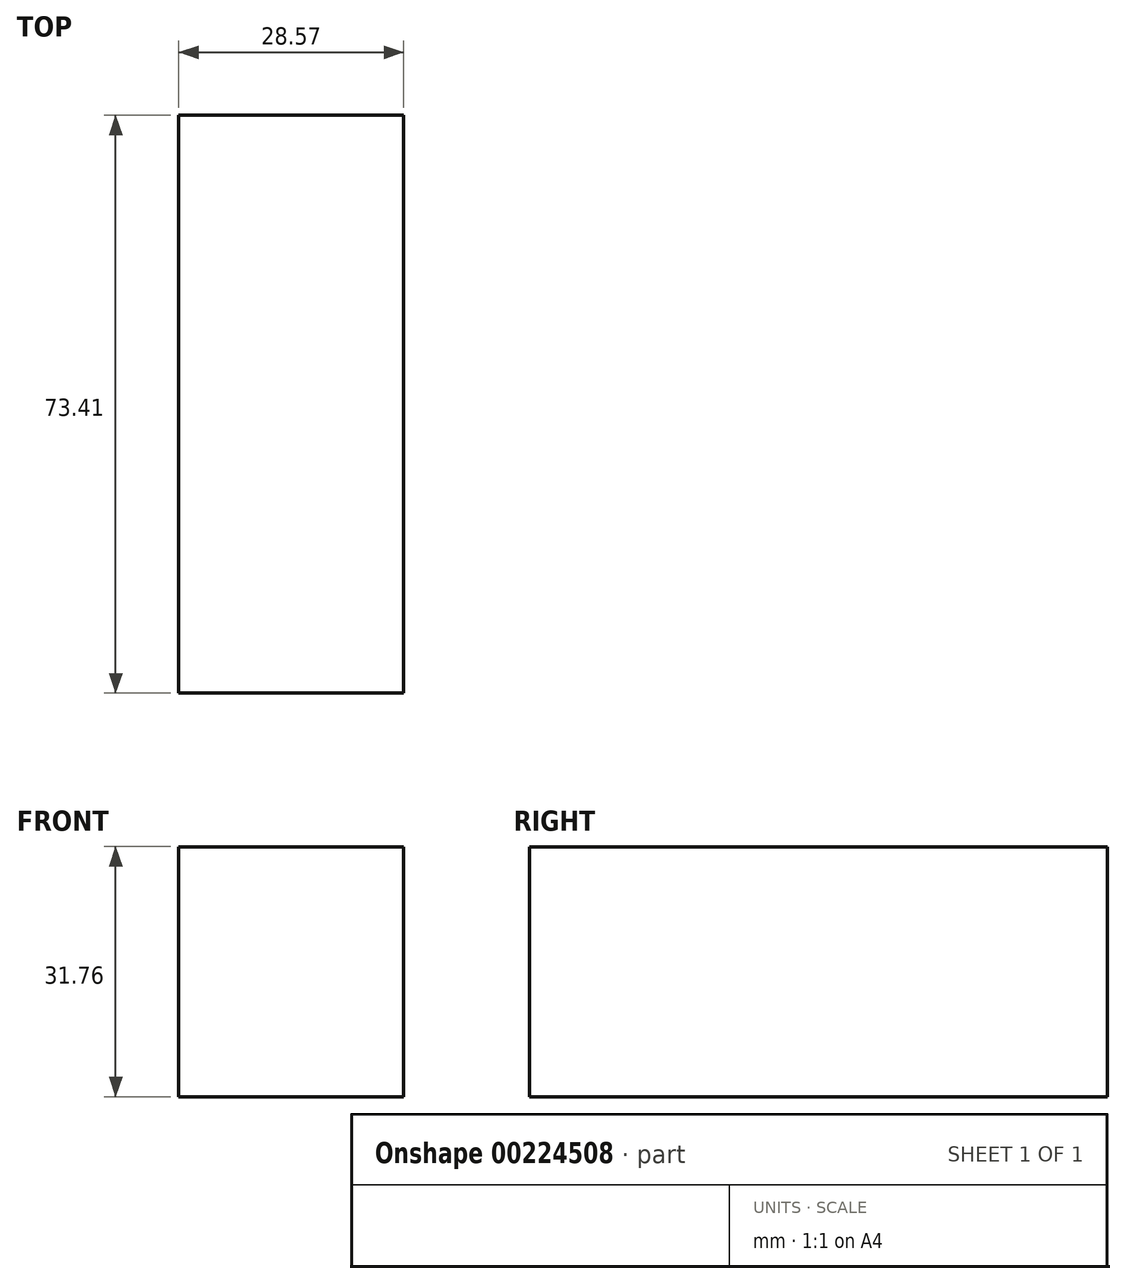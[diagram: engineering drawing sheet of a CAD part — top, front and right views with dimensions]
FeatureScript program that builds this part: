
annotation { "Feature Type Name" : "Feature", "Feature Type Description" : "" }
export const myFeature = defineFeature(function(context is Context, id is Id, definition is map)
    precondition{}
    {
        {
            var Q0;
            Q0=qCreatedBy(makeId("Front.planeOp"),FACE);
            var sketch = newSketch(context, id + "F0", { "sketchPlane" : qUnion([Q0])});
            skLineSegment(sketch, "E0", {"start": v(0, 0) * mm, "end": v(0, 15.88) * mm});
            skLineSegment(sketch, "E1", {"start": v(0, 15.88) * mm, "end": v(0, -15.87) * mm});
            skLineSegment(sketch, "E2", {"start": v(0, 15.88) * mm, "end": v(28.58, 15.88) * mm});
            skLineSegment(sketch, "E3.MirrorCS", {"start": v(0, -15.88) * mm, "end": v(0, 15.87) * mm});
            skLineSegment(sketch, "E4.MirrorCS", {"start": v(0, -15.88) * mm, "end": v(28.58, -15.88) * mm});
            skLineSegment(sketch, "E5", {"start": v(28.58, 15.88) * mm, "end": v(28.58, -15.88) * mm});
            skSolve(sketch);
        }
        {
            var Q0;
            {var subQ0=sQuery(id+"F0.wireOp",EDGE,"E2");Q0=makeQuery(id+"F0.imprint","IMPRINT",FACE,{"disambiguationData":[TD([[makeQuery(id+"F0.imprint","IMPRINT",EDGE,{"derivedFrom":subQ0}),-1.0]])]});}
            extrude(context, id + "F1", {"entities" : qUnion([Q0]), "depth" : 73.4 * mm});
        }
    });
